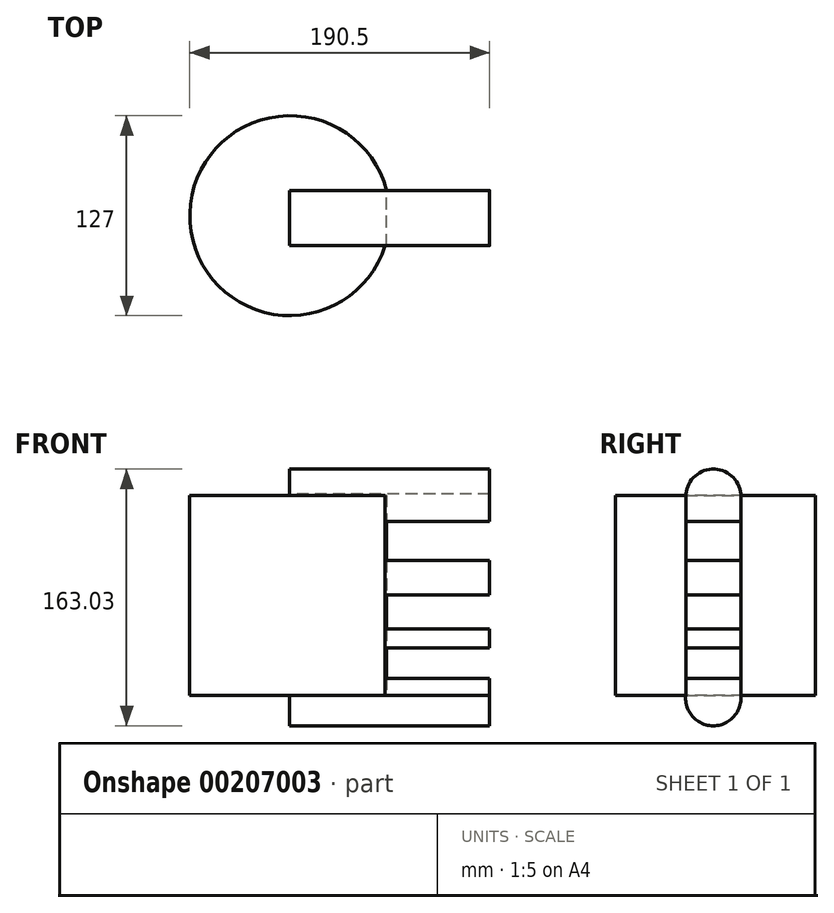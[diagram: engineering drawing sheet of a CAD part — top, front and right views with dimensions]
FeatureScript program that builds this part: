
annotation { "Feature Type Name" : "Feature", "Feature Type Description" : "" }
export const myFeature = defineFeature(function(context is Context, id is Id, definition is map)
    precondition{}
    {
        {
            var Q0;
            Q0=qCreatedBy(makeId("Top.planeOp"),FACE);
            var sketch = newSketch(context, id + "F0", { "sketchPlane" : qUnion([Q0])});
            skCircle(sketch, "E0", {"center": v(0, 0) * mm, "radius": 63.5 * mm});
            skSolve(sketch);
        }
        {
            var Q0;
            Q0=makeQuery(id+"F0.imprint","IMPRINT",FACE,{"disambiguationData":[TD([[makeQuery(id+"F0.imprint","IMPRINT",EDGE,{"derivedFrom":sQuery(id+"F0.wireOp",EDGE,"E0")}),1.0]])]});
            extrude(context, id + "F1", {"entities" : qUnion([Q0]), "depth" : 127 * mm});
        }
        {
            var Q0;
            Q0=qCreatedBy(makeId("Right.planeOp"),FACE);
            var sketch = newSketch(context, id + "F2", { "sketchPlane" : qUnion([Q0])});
            skLineSegment(sketch, "E1", {"start": v(-19.03, 126.13) * mm, "end": v(-19.03, 0) * mm});
            skLineSegment(sketch, "E2", {"start": v(15.98, 127.77) * mm, "end": v(15.98, 0) * mm});
            skArc(sketch, "E3", {"start": v(15.98, 127.77) * mm, "mid": v(-2.3, 143.65) * mm, "end": v(-19.03, 126.13) * mm});
            skArc(sketch, "E4", {"start": v(-19.03, 0) * mm, "mid": v(-1.52, -19.36) * mm, "end": v(15.98, 0) * mm});
            skSolve(sketch);
        }
        {
            var Q0;
            Q0=makeQuery(id+"F2.imprint","IMPRINT",FACE,{"disambiguationData":[TD([[makeQuery(id+"F2.imprint","IMPRINT",EDGE,{"derivedFrom":sQuery(id+"F2.wireOp",EDGE,"E1")}),1.0]])]});
            extrude(context, id + "F3", {"entities" : qUnion([Q0]), "operationType" : NewBodyOperationType.ADD, "depth" : 127 * mm});
        }
        {
            var Q0;
            Q0=makeQuery(id+"F3.opExtrude","SWEPT_FACE",FACE,{"disambiguationData":[OSD([sQuery(id+"F2.wireOp",EDGE,"E2")])]});
            var sketch = newSketch(context, id + "F4", { "sketchPlane" : qUnion([Q0])});
            skLineSegment(sketch, "E5.bottom", {"start": v(-127, 110.53) * mm, "end": v(-61.46, 110.53) * mm});
            skLineSegment(sketch, "E5.top", {"start": v(-127, 85.62) * mm, "end": v(-61.46, 85.62) * mm});
            skLineSegment(sketch, "E5.left", {"start": v(-127, 110.53) * mm, "end": v(-127, 85.62) * mm});
            skLineSegment(sketch, "E5.right", {"start": v(-61.46, 110.53) * mm, "end": v(-61.46, 85.62) * mm});
            skLineSegment(sketch, "E6.bottom", {"start": v(-127, 63.89) * mm, "end": v(-61.46, 63.89) * mm});
            skLineSegment(sketch, "E6.top", {"start": v(-127, 42.16) * mm, "end": v(-61.46, 42.16) * mm});
            skLineSegment(sketch, "E6.left", {"start": v(-127, 63.89) * mm, "end": v(-127, 42.16) * mm});
            skLineSegment(sketch, "E6.right", {"start": v(-61.46, 63.89) * mm, "end": v(-61.46, 42.16) * mm});
            skLineSegment(sketch, "E7.bottom", {"start": v(-127, 29.99) * mm, "end": v(-61.46, 29.99) * mm});
            skLineSegment(sketch, "E7.top", {"start": v(-127, 10.86) * mm, "end": v(-61.46, 10.86) * mm});
            skLineSegment(sketch, "E7.left", {"start": v(-127, 29.99) * mm, "end": v(-127, 10.86) * mm});
            skLineSegment(sketch, "E7.right", {"start": v(-61.46, 29.99) * mm, "end": v(-61.46, 10.86) * mm});
            skSolve(sketch);
        }
        {
            var Q0;
            Q0=makeQuery(id+"F4.imprint","IMPRINT",FACE,{"disambiguationData":[TD([[makeQuery(id+"F4.imprint","IMPRINT",EDGE,{"derivedFrom":sQuery(id+"F4.wireOp",EDGE,"E5.bottom")}),-1.0]])]});
            var Q1;
            Q1=makeQuery(id+"F4.imprint","IMPRINT",FACE,{"disambiguationData":[TD([[makeQuery(id+"F4.imprint","IMPRINT",EDGE,{"derivedFrom":sQuery(id+"F4.wireOp",EDGE,"E6.bottom")}),-1.0]])]});
            var Q2;
            Q2=makeQuery(id+"F4.imprint","IMPRINT",FACE,{"disambiguationData":[TD([[makeQuery(id+"F4.imprint","IMPRINT",EDGE,{"derivedFrom":sQuery(id+"F4.wireOp",EDGE,"E7.bottom")}),-1.0]])]});
            extrude(context, id + "F5", {"entities" : qUnion([Q0, Q1, Q2]), "operationType" : NewBodyOperationType.REMOVE, "oppositeDirection" : true, "depth" : 35.56 * mm});
        }
    });
